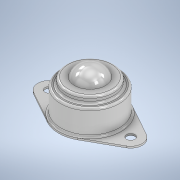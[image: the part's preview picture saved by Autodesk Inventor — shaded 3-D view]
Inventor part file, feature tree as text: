
AUTODESK INVENTOR PART (.ipt)
format: ipt  version: 2020.2 (Build 242310000, 310)  size: 243,200 bytes
history: native  units: mm
features: sketch x4, revolve x2, extrude x2
ambient origin geometry x8: Origin, YZ Plane, XZ Plane, XY Plane, X Axis, Y Axis, Z Axis, Center Point
bodies: Solid1 (feature_tree)
feature tree (8):
  revolve  "Revolution1"  [1 undecoded]
  extrude  "Extrusion1"  Depth=0.8mm
  extrude  "Extrusion2"  Depth=13.0625mm
  revolve  "Revolution2"  [1 undecoded]
  sketch  "Sketch1"  dims[d0=14.0mm d1=15.875mm]
  sketch  "Sketch2"  dims[d2=25.0mm d3=0.8mm]
  sketch  "Sketch3"  dims[d4=16.0mm d5=13.0625mm]
  sketch  "Sketch5"  dims[d6=1.0mm d8=1.4mm d9=1.0mm d10=0.5mm d11=90.0deg d12=39.0mm d13=4.0mm d14=4.0mm d15=19.5mm d16=10.0mm d17=0.0mm d18=15.2mm d19=0.0mm d20=13.063mm d21=15.875mm d22=90.0deg]
note: 2 required parameter values undecoded (feature->parameter linkage not recoverable at this tier; creation-order binding heuristic only, values carry confidence <= 0.55)
